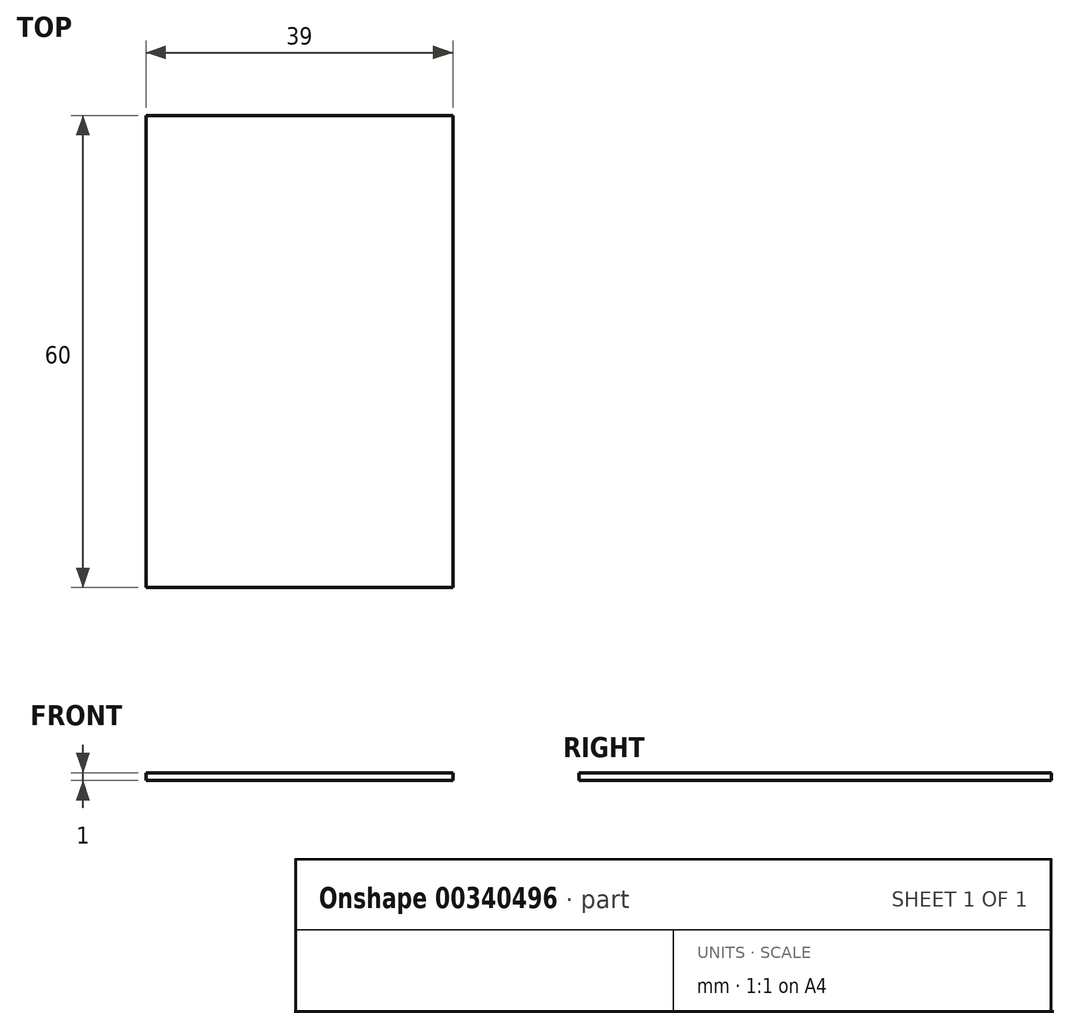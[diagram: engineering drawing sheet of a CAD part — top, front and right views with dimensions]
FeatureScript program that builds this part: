
annotation { "Feature Type Name" : "Feature", "Feature Type Description" : "" }
export const myFeature = defineFeature(function(context is Context, id is Id, definition is map)
    precondition{}
    {
        {
            var Q0;
            Q0=qCreatedBy(makeId("Top.planeOp"),FACE);
            var sketch = newSketch(context, id + "F0", { "sketchPlane" : qUnion([Q0])});
            skLineSegment(sketch, "E0.bottom", {"start": v(19.5, -30) * mm, "end": v(-19.5, -30) * mm});
            skLineSegment(sketch, "E0.top", {"start": v(19.5, 30) * mm, "end": v(-19.5, 30) * mm});
            skLineSegment(sketch, "E0.left", {"start": v(19.5, -30) * mm, "end": v(19.5, 30) * mm});
            skLineSegment(sketch, "E0.right", {"start": v(-19.5, -30) * mm, "end": v(-19.5, 30) * mm});
            skPoint(sketch, "E0.middle", {"position": v(0, 0) * mm});
            skSolve(sketch);
        }
        {
            var Q0;
            Q0=qSketchRegion(id+"F0",true);
            extrude(context, id + "F1", {"entities" : qUnion([Q0]), "depth" : 1 * mm});
        }
    });
